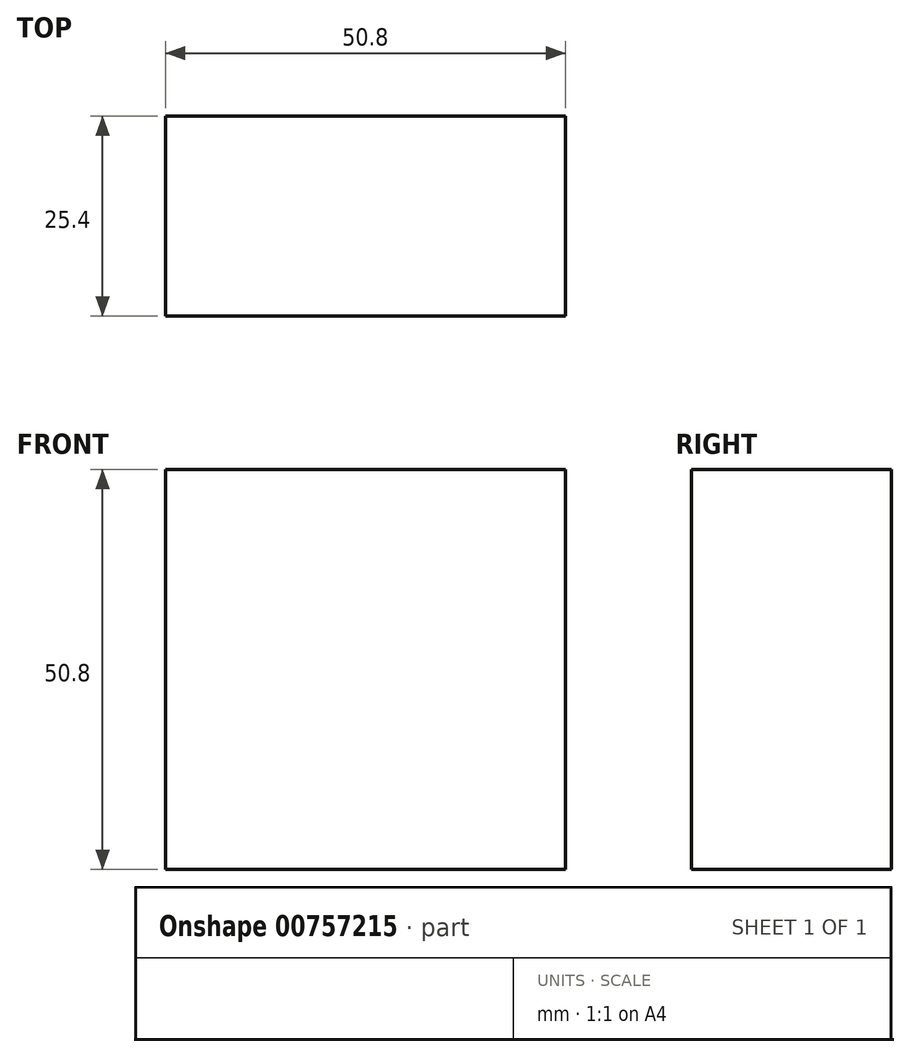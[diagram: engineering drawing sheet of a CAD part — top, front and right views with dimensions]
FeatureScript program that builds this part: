
annotation { "Feature Type Name" : "Feature", "Feature Type Description" : "" }
export const myFeature = defineFeature(function(context is Context, id is Id, definition is map)
    precondition{}
    {
        {
            var Q0;
            Q0=qCreatedBy(makeId("Top.planeOp"),FACE);
            var sketch = newSketch(context, id + "F0", { "sketchPlane" : qUnion([Q0])});
            skLineSegment(sketch, "E0.bottom", {"start": v(-49.32, -9.92) * mm, "end": v(1.48, -9.92) * mm});
            skLineSegment(sketch, "E0.top", {"start": v(-49.32, 15.48) * mm, "end": v(1.48, 15.48) * mm});
            skLineSegment(sketch, "E0.left", {"start": v(-49.32, -9.92) * mm, "end": v(-49.32, 15.48) * mm});
            skLineSegment(sketch, "E0.right", {"start": v(1.48, -9.92) * mm, "end": v(1.48, 15.48) * mm});
            skSolve(sketch);
        }
        {
            var Q0;
            Q0 = qSketchRegion(id + "F0", true);
            extrude(context, id + "F1", {"entities" : qUnion([Q0]), "depth" : 50.8 * mm, "offsetDistance" : 25.4 * mm});
        }
    });
